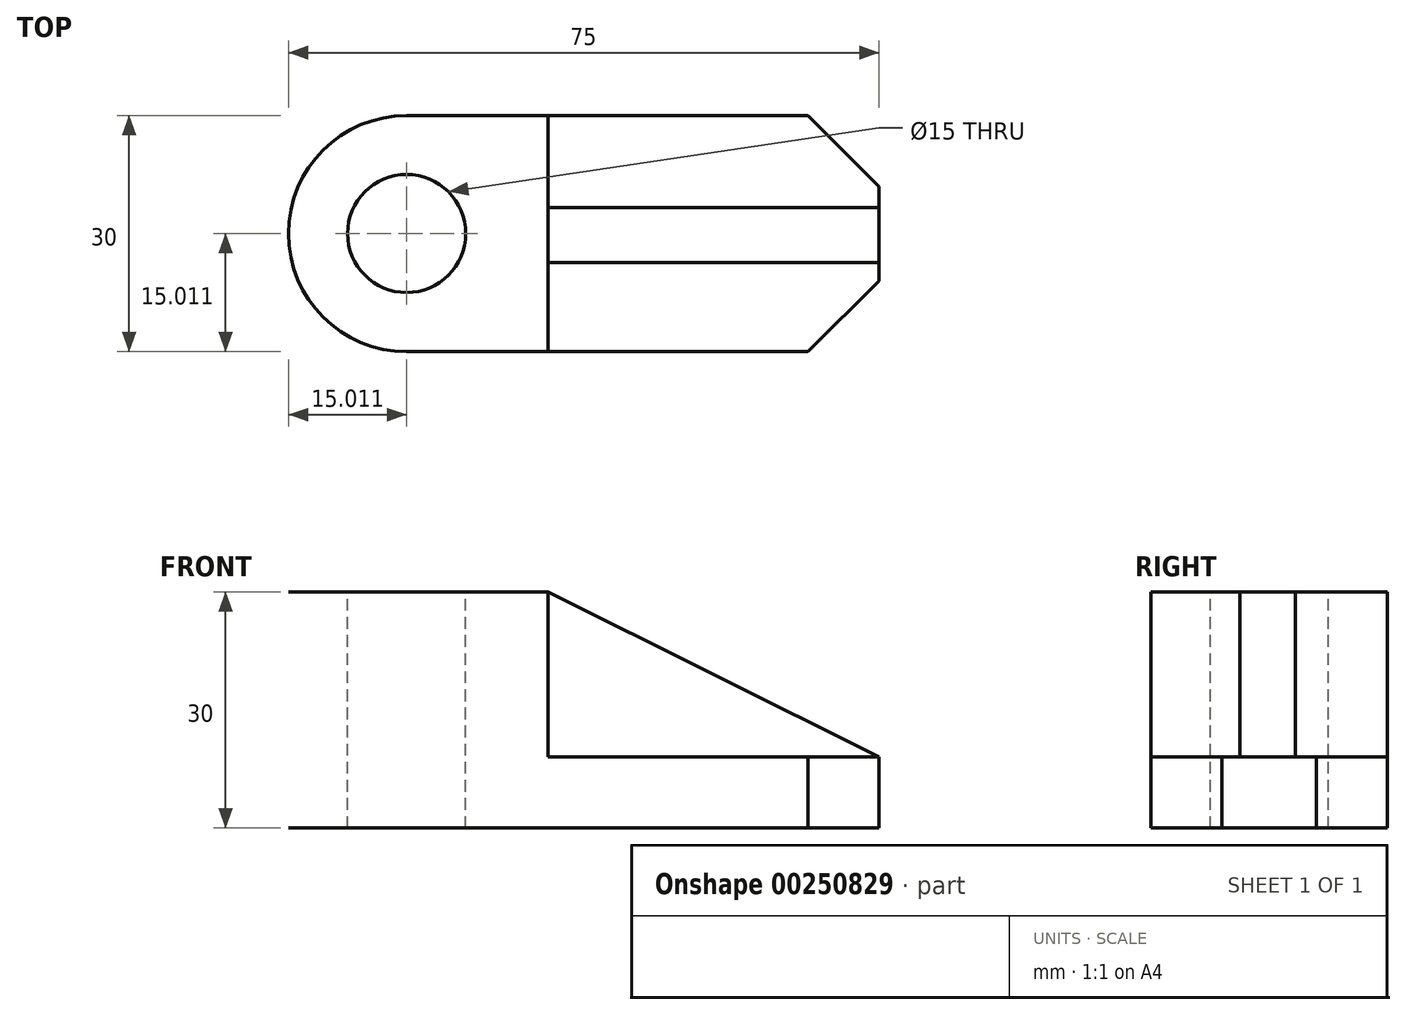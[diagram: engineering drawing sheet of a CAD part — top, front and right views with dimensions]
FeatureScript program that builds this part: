
annotation { "Feature Type Name" : "Feature", "Feature Type Description" : "" }
export const myFeature = defineFeature(function(context is Context, id is Id, definition is map)
    precondition{}
    {
        {
            var Q0;
            Q0=qCreatedBy(makeId("Top.planeOp"),FACE);
            var sketch = newSketch(context, id + "F0", { "sketchPlane" : qUnion([Q0])});
            skLineSegment(sketch, "E0", {"start": v(0, 0) * mm, "end": v(45, 0) * mm});
            skLineSegment(sketch, "E1", {"start": v(45, 0) * mm, "end": v(45, 30) * mm});
            skLineSegment(sketch, "E2", {"start": v(45, 30) * mm, "end": v(-30, 30) * mm});
            skLineSegment(sketch, "E3", {"start": v(-30, 30) * mm, "end": v(-30, 0) * mm});
            skLineSegment(sketch, "E4", {"start": v(-30, 0) * mm, "end": v(0, 0) * mm});
            skSolve(sketch);
        }
        {
            var Q0;
            Q0=makeQuery(id+"F0.imprint","IMPRINT",FACE,{"disambiguationData":[TD([[makeQuery(id+"F0.imprint","IMPRINT",EDGE,{"derivedFrom":sQuery(id+"F0.wireOp",EDGE,"E0")}),1.0]])]});
            extrude(context, id + "F1", {"entities" : qUnion([Q0]), "depth" : 9 * mm});
        }
        {
            var Q0;
            Q0=makeQuery(id+"F1.opExtrude","CAP_FACE",FACE,{"disambiguationData":[OSD([sQuery(id+"F0.wireOp",EDGE,"E0"),sQuery(id+"F0.wireOp",EDGE,"E1"),sQuery(id+"F0.wireOp",EDGE,"E2"),sQuery(id+"F0.wireOp",EDGE,"E3"),sQuery(id+"F0.wireOp",EDGE,"E4")])],"isStart":false});
            var sketch = newSketch(context, id + "F2", { "sketchPlane" : qUnion([Q0])});
            skLineSegment(sketch, "E5", {"start": v(3, 0) * mm, "end": v(3, 30) * mm});
            skLineSegment(sketch, "E6", {"start": v(3, 30) * mm, "end": v(-30, 30) * mm});
            skLineSegment(sketch, "E7", {"start": v(-30, 30) * mm, "end": v(-30, 0) * mm});
            skLineSegment(sketch, "E8", {"start": v(-30, 0) * mm, "end": v(3, 0) * mm});
            skSolve(sketch);
        }
        {
            var Q0;
            Q0=makeQuery(id+"F2.imprint","IMPRINT",FACE,{"disambiguationData":[TD([[makeQuery(id+"F2.imprint","IMPRINT",EDGE,{"derivedFrom":sQuery(id+"F2.wireOp",EDGE,"E5")}),1.0]])]});
            extrude(context, id + "F3", {"entities" : qUnion([Q0]), "operationType" : NewBodyOperationType.ADD, "depth" : 21 * mm});
        }
        {
            var Q0;
            Q0=makeQuery(id+"F3.boolean.opBoolean","MERGE",EDGE,{"derivedFrom":[makeQuery(id+"F1.opExtrude","SWEPT_EDGE",EDGE,{"disambiguationData":[OSD([sQuery(id+"F0.wireOp",EDGE,"E3"),sQuery(id+"F0.wireOp",EDGE,"E4")])]}),makeQuery(id+"F3.opExtrude","SWEPT_EDGE",EDGE,{"disambiguationData":[OSD([sQuery(id+"F2.wireOp",EDGE,"E7"),sQuery(id+"F2.wireOp",EDGE,"E8")])]})]});
            var Q1;
            Q1=makeQuery(id+"F3.boolean.opBoolean","MERGE",EDGE,{"derivedFrom":[makeQuery(id+"F1.opExtrude","SWEPT_EDGE",EDGE,{"disambiguationData":[OSD([sQuery(id+"F0.wireOp",EDGE,"E2"),sQuery(id+"F0.wireOp",EDGE,"E3")])]}),makeQuery(id+"F3.opExtrude","SWEPT_EDGE",EDGE,{"disambiguationData":[OSD([sQuery(id+"F2.wireOp",EDGE,"E6"),sQuery(id+"F2.wireOp",EDGE,"E7")])]})]});
            fillet(context, id + "F4", {"entities" : qUnion([Q0, Q1]), "radius" : 15 * mm, "tangentPropagation" : true, "allowEdgeOverflow" : false});
        }
        {
            var Q0;
            Q0=makeQuery(id+"F1.opExtrude","SWEPT_EDGE",EDGE,{"disambiguationData":[OSD([sQuery(id+"F0.wireOp",EDGE,"E0"),sQuery(id+"F0.wireOp",EDGE,"E1")])]});
            var Q1;
            Q1=makeQuery(id+"F1.opExtrude","SWEPT_EDGE",EDGE,{"disambiguationData":[OSD([sQuery(id+"F0.wireOp",EDGE,"E1"),sQuery(id+"F0.wireOp",EDGE,"E2")])]});
            chamfer(context, id + "F5", {"entities" : qUnion([Q0, Q1]), "chamferType" : ChamferType.TWO_OFFSETS, "width1" : 9 * mm, "oppositeDirection" : false, "width2" : 9 * mm, "tangentPropagation" : true});
        }
        {
            var Q0;
            Q0=makeQuery(id+"F1.opExtrude","CAP_FACE",FACE,{"disambiguationData":[OSD([sQuery(id+"F0.wireOp",EDGE,"E0"),sQuery(id+"F0.wireOp",EDGE,"E1"),sQuery(id+"F0.wireOp",EDGE,"E2"),sQuery(id+"F0.wireOp",EDGE,"E3"),sQuery(id+"F0.wireOp",EDGE,"E4")])],"isStart":false});
            var sketch = newSketch(context, id + "F6", { "sketchPlane" : qUnion([Q0])});
            skLineSegment(sketch, "E9", {"start": v(45, 18.3) * mm, "end": v(3, 18.3) * mm});
            skLineSegment(sketch, "E10", {"start": v(45, 11.3) * mm, "end": v(3, 11.3) * mm});
            skLineSegment(sketch, "E11", {"start": v(3, 11.3) * mm, "end": v(3, 18.3) * mm});
            skLineSegment(sketch, "E12", {"start": v(45, 11.3) * mm, "end": v(45, 18.3) * mm});
            skSolve(sketch);
        }
        {
            var Q0;
            Q0=makeQuery(id+"F6.imprint","IMPRINT",FACE,{"disambiguationData":[TD([[makeQuery(id+"F6.imprint","IMPRINT",EDGE,{"derivedFrom":sQuery(id+"F6.wireOp",EDGE,"E9")}),1.0]])]});
            extrude(context, id + "F7", {"entities" : qUnion([Q0]), "operationType" : NewBodyOperationType.ADD, "depth" : 21 * mm});
        }
        {
            var Q0;
            Q0=makeQuery(id+"F7.opExtrude","SWEPT_FACE",FACE,{"disambiguationData":[OSD([sQuery(id+"F6.wireOp",EDGE,"E10")])]});
            var sketch = newSketch(context, id + "F8", { "sketchPlane" : qUnion([Q0])});
            skLineSegment(sketch, "E13", {"start": v(3, 30) * mm, "end": v(45, 9) * mm});
            skSolve(sketch);
        }
        {
            var Q0;
            Q0=makeQuery(id+"F8.imprint","IMPRINT",FACE,{"disambiguationData":[TD([[makeQuery(id+"F8.imprint","IMPRINT",EDGE,{"derivedFrom":sQuery(id+"F8.wireOp",EDGE,"E13")}),1.0]])]});
            extrude(context, id + "F9", {"entities" : qUnion([Q0]), "operationType" : NewBodyOperationType.REMOVE, "endBound" : BoundingType.THROUGH_ALL, "oppositeDirection" : true, "depth" : 25.4 * mm});
        }
        {
            var Q0;
            Q0=makeQuery(id+"F7.boolean.opBoolean","MERGE",FACE,{"derivedFrom":[makeQuery(id+"F3.opExtrude","CAP_FACE",FACE,{"disambiguationData":[OSD([sQuery(id+"F2.wireOp",EDGE,"E5"),sQuery(id+"F2.wireOp",EDGE,"E6"),sQuery(id+"F2.wireOp",EDGE,"E7"),sQuery(id+"F2.wireOp",EDGE,"E8")])],"isStart":false}),makeQuery(id+"F7.opExtrude","CAP_FACE",FACE,{"disambiguationData":[OSD([sQuery(id+"F6.wireOp",EDGE,"E9"),sQuery(id+"F6.wireOp",EDGE,"E10"),sQuery(id+"F6.wireOp",EDGE,"E11"),sQuery(id+"F6.wireOp",EDGE,"E12")])],"isStart":false})]});
            var sketch = newSketch(context, id + "F10", { "sketchPlane" : qUnion([Q0])});
            skCircle(sketch, "E14", {"center": v(-14.99, 15.01) * mm, "radius": 7.5 * mm});
            skSolve(sketch);
        }
        {
            var Q0;
            Q0=makeQuery(id+"F10.imprint","IMPRINT",FACE,{"disambiguationData":[TD([[makeQuery(id+"F10.imprint","IMPRINT",EDGE,{"derivedFrom":sQuery(id+"F10.wireOp",EDGE,"E14")}),1.0]])]});
            extrude(context, id + "F11", {"entities" : qUnion([Q0]), "operationType" : NewBodyOperationType.REMOVE, "endBound" : BoundingType.THROUGH_ALL, "oppositeDirection" : true, "depth" : 25.4 * mm});
        }
    });
